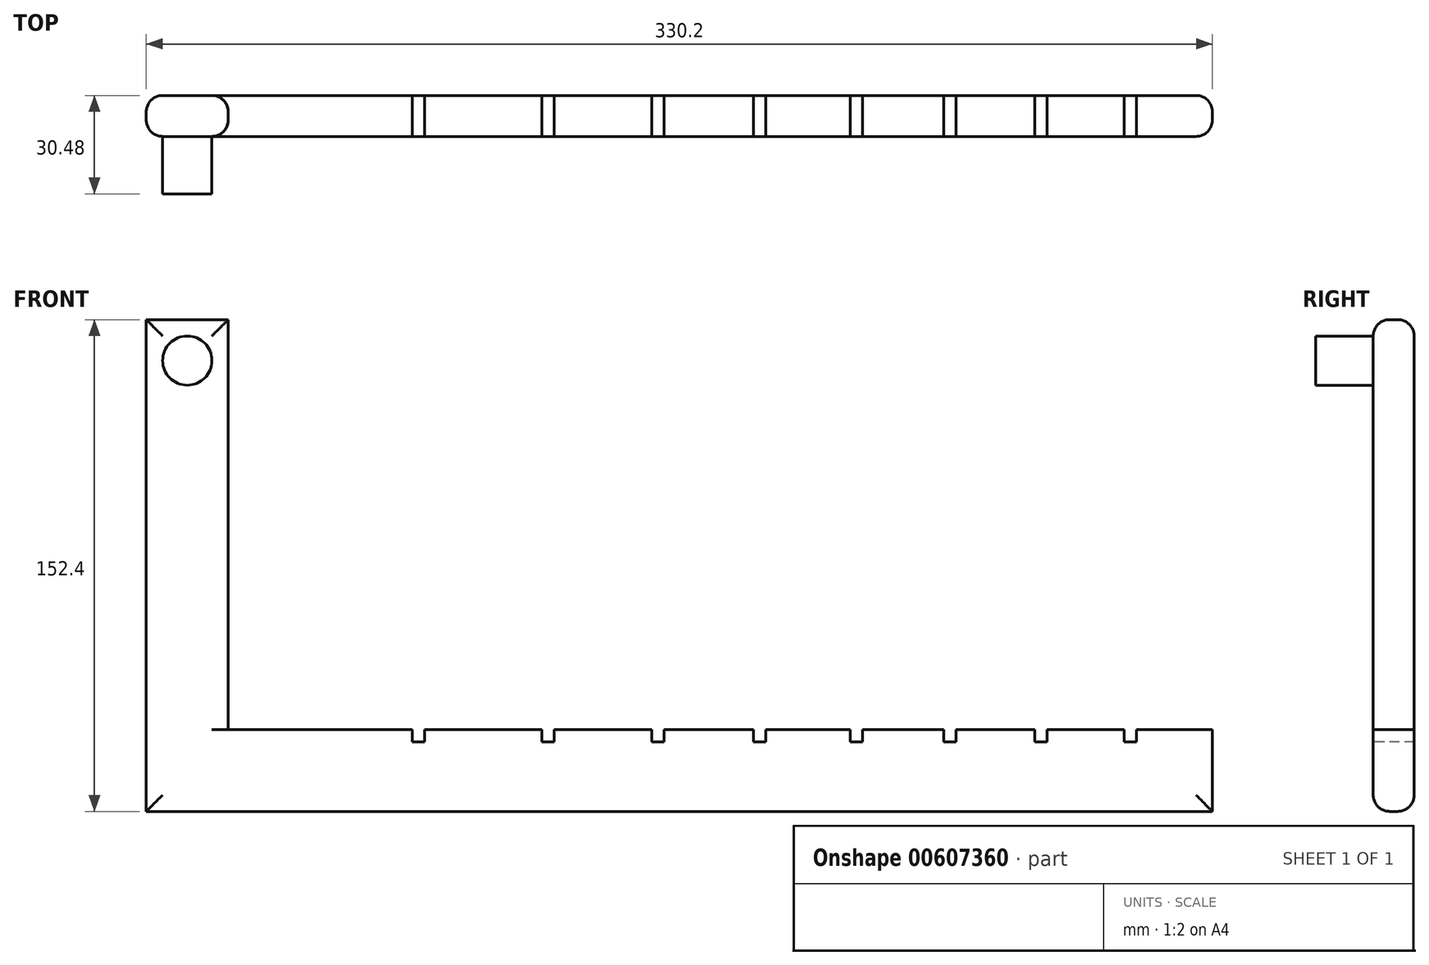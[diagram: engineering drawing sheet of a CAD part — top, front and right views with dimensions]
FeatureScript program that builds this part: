
annotation { "Feature Type Name" : "Feature", "Feature Type Description" : "" }
export const myFeature = defineFeature(function(context is Context, id is Id, definition is map)
    precondition{}
    {
        {
            var Q0;
            Q0=qCreatedBy(makeId("Front.planeOp"),FACE);
            var sketch = newSketch(context, id + "F0", { "sketchPlane" : qUnion([Q0])});
            skLineSegment(sketch, "E0.bottom", {"start": v(0, 0) * mm, "end": v(330.2, 0) * mm});
            skLineSegment(sketch, "E0.top", {"start": v(0, -25.4) * mm, "end": v(330.2, -25.4) * mm});
            skLineSegment(sketch, "E0.left", {"start": v(0, 0) * mm, "end": v(0, -25.4) * mm});
            skLineSegment(sketch, "E0.right", {"start": v(330.2, 0) * mm, "end": v(330.2, -25.4) * mm});
            skLineSegment(sketch, "E1.bottom", {"start": v(0, 0) * mm, "end": v(25.4, 0) * mm});
            skLineSegment(sketch, "E1.top", {"start": v(0, 127) * mm, "end": v(25.4, 127) * mm});
            skLineSegment(sketch, "E1.left", {"start": v(0, 0) * mm, "end": v(0, 127) * mm});
            skLineSegment(sketch, "E1.right", {"start": v(25.4, 0) * mm, "end": v(25.4, 127) * mm});
            skSolve(sketch);
        }
        {
            var Q0;
            Q0 = qSketchRegion(id + "F0", true);
            extrude(context, id + "F1", {"entities" : qUnion([Q0]), "depth" : 12.7 * mm, "offsetDistance" : 25.4 * mm});
        }
        {
            var Q0;
            Q0=makeQuery(id+"F1.opExtrude","CAP_FACE",FACE,{"disambiguationData":[OSD([sQuery(id+"F0.wireOp",EDGE,"E0.bottom"),sQuery(id+"F0.wireOp",EDGE,"E0.top"),sQuery(id+"F0.wireOp",EDGE,"E0.left"),sQuery(id+"F0.wireOp",EDGE,"E0.right"),sQuery(id+"F0.wireOp",EDGE,"E1.top"),sQuery(id+"F0.wireOp",EDGE,"E1.left"),sQuery(id+"F0.wireOp",EDGE,"E1.right")])],"isStart":false});
            var sketch = newSketch(context, id + "F2", { "sketchPlane" : qUnion([Q0])});
            skPoint(sketch, "E2", {"position": v(12.7, 127) * mm});
            skLineSegment(sketch, "E3", {"start": v(12.7, 127) * mm, "end": v(12.7, 114.3) * mm});
            skCircle(sketch, "E4", {"center": v(12.7, 114.3) * mm, "radius": 7.62 * mm});
            skSolve(sketch);
        }
        {
            var Q0;
            Q0 = qSketchRegion(id + "F2", true);
            extrude(context, id + "F3", {"entities" : qUnion([Q0]), "operationType" : NewBodyOperationType.ADD, "depth" : 17.78 * mm, "offsetDistance" : 25.4 * mm});
        }
        {
            var Q0;
            Q0=makeQuery(id+"F1.opExtrude","CAP_FACE",FACE,{"disambiguationData":[OSD([sQuery(id+"F0.wireOp",EDGE,"E0.bottom"),sQuery(id+"F0.wireOp",EDGE,"E0.top"),sQuery(id+"F0.wireOp",EDGE,"E0.left"),sQuery(id+"F0.wireOp",EDGE,"E0.right"),sQuery(id+"F0.wireOp",EDGE,"E1.top"),sQuery(id+"F0.wireOp",EDGE,"E1.left"),sQuery(id+"F0.wireOp",EDGE,"E1.right")])],"isStart":false});
            var sketch = newSketch(context, id + "F4", { "sketchPlane" : qUnion([Q0])});
            skLineSegment(sketch, "E5", {"start": v(25.4, 0) * mm, "end": v(84.33, 0) * mm});
            skLineSegment(sketch, "E6", {"start": v(25.4, 0) * mm, "end": v(124.46, 0) * mm});
            skLineSegment(sketch, "E7", {"start": v(25.4, 0) * mm, "end": v(158.5, 0) * mm});
            skLineSegment(sketch, "E8", {"start": v(25.4, 0) * mm, "end": v(190, 0) * mm});
            skLineSegment(sketch, "E9", {"start": v(25.4, 0) * mm, "end": v(219.96, 0) * mm});
            skLineSegment(sketch, "E10", {"start": v(25.4, 0) * mm, "end": v(248.92, 0) * mm});
            skLineSegment(sketch, "E11", {"start": v(25.4, 0) * mm, "end": v(277.11, 0) * mm});
            skLineSegment(sketch, "E12", {"start": v(25.4, 0) * mm, "end": v(304.8, 0) * mm});
            skLineSegment(sketch, "E13.bottom", {"start": v(86.23, -3.8) * mm, "end": v(82.42, -3.8) * mm});
            skLineSegment(sketch, "E13.top", {"start": v(86.23, 3.81) * mm, "end": v(82.42, 3.81) * mm});
            skLineSegment(sketch, "E13.left", {"start": v(86.23, -3.8) * mm, "end": v(86.23, 3.81) * mm});
            skLineSegment(sketch, "E13.right", {"start": v(82.42, -3.8) * mm, "end": v(82.42, 3.81) * mm});
            skPoint(sketch, "E13.middle", {"position": v(84.33, 0) * mm});
            skLineSegment(sketch, "E14.bottom", {"start": v(126.37, -3.8) * mm, "end": v(122.56, -3.8) * mm});
            skLineSegment(sketch, "E14.top", {"start": v(126.37, 3.81) * mm, "end": v(122.56, 3.81) * mm});
            skLineSegment(sketch, "E14.left", {"start": v(126.37, -3.8) * mm, "end": v(126.37, 3.81) * mm});
            skLineSegment(sketch, "E14.right", {"start": v(122.56, -3.8) * mm, "end": v(122.56, 3.81) * mm});
            skPoint(sketch, "E14.middle", {"position": v(124.46, 0) * mm});
            skLineSegment(sketch, "E15.bottom", {"start": v(160.4, -3.8) * mm, "end": v(156.6, -3.8) * mm});
            skLineSegment(sketch, "E15.top", {"start": v(160.4, 3.81) * mm, "end": v(156.6, 3.81) * mm});
            skLineSegment(sketch, "E15.left", {"start": v(160.4, -3.8) * mm, "end": v(160.4, 3.81) * mm});
            skLineSegment(sketch, "E15.right", {"start": v(156.6, -3.8) * mm, "end": v(156.6, 3.81) * mm});
            skPoint(sketch, "E15.middle", {"position": v(158.5, 0) * mm});
            skLineSegment(sketch, "E16.bottom", {"start": v(191.9, -3.8) * mm, "end": v(188.09, -3.8) * mm});
            skLineSegment(sketch, "E16.top", {"start": v(191.9, 3.81) * mm, "end": v(188.09, 3.81) * mm});
            skLineSegment(sketch, "E16.left", {"start": v(191.9, -3.8) * mm, "end": v(191.9, 3.81) * mm});
            skLineSegment(sketch, "E16.right", {"start": v(188.09, -3.8) * mm, "end": v(188.09, 3.81) * mm});
            skPoint(sketch, "E16.middle", {"position": v(190, 0) * mm});
            skLineSegment(sketch, "E17.bottom", {"start": v(221.87, -3.8) * mm, "end": v(218.06, -3.8) * mm});
            skLineSegment(sketch, "E17.top", {"start": v(221.87, 3.81) * mm, "end": v(218.06, 3.81) * mm});
            skLineSegment(sketch, "E17.left", {"start": v(221.87, -3.8) * mm, "end": v(221.87, 3.81) * mm});
            skLineSegment(sketch, "E17.right", {"start": v(218.06, -3.8) * mm, "end": v(218.06, 3.81) * mm});
            skPoint(sketch, "E17.middle", {"position": v(219.96, 0) * mm});
            skLineSegment(sketch, "E18.bottom", {"start": v(250.83, -3.8) * mm, "end": v(247.02, -3.8) * mm});
            skLineSegment(sketch, "E18.top", {"start": v(250.83, 3.81) * mm, "end": v(247.02, 3.81) * mm});
            skLineSegment(sketch, "E18.left", {"start": v(250.83, -3.8) * mm, "end": v(250.83, 3.81) * mm});
            skLineSegment(sketch, "E18.right", {"start": v(247.02, -3.8) * mm, "end": v(247.02, 3.81) * mm});
            skPoint(sketch, "E18.middle", {"position": v(248.92, 0) * mm});
            skLineSegment(sketch, "E19.bottom", {"start": v(279.02, -3.8) * mm, "end": v(275.2, -3.8) * mm});
            skLineSegment(sketch, "E19.top", {"start": v(279.02, 3.81) * mm, "end": v(275.2, 3.81) * mm});
            skLineSegment(sketch, "E19.left", {"start": v(279.02, -3.8) * mm, "end": v(279.02, 3.81) * mm});
            skLineSegment(sketch, "E19.right", {"start": v(275.2, -3.8) * mm, "end": v(275.2, 3.81) * mm});
            skPoint(sketch, "E19.middle", {"position": v(277.11, 0) * mm});
            skLineSegment(sketch, "E20.bottom", {"start": v(306.7, -3.8) * mm, "end": v(302.9, -3.8) * mm});
            skLineSegment(sketch, "E20.top", {"start": v(306.7, 3.81) * mm, "end": v(302.9, 3.81) * mm});
            skLineSegment(sketch, "E20.left", {"start": v(306.7, -3.8) * mm, "end": v(306.7, 3.81) * mm});
            skLineSegment(sketch, "E20.right", {"start": v(302.9, -3.8) * mm, "end": v(302.9, 3.81) * mm});
            skPoint(sketch, "E20.middle", {"position": v(304.8, 0) * mm});
            skSolve(sketch);
        }
        {
            var Q0;
            Q0 = qSketchRegion(id + "F4", true);
            extrude(context, id + "F5", {"entities" : qUnion([Q0]), "operationType" : NewBodyOperationType.REMOVE, "oppositeDirection" : true, "depth" : 25.4 * mm, "offsetDistance" : 25.4 * mm});
        }
        {
            var Q0;
            Q0=makeQuery(id+"F1.opExtrude","CAP_EDGE",EDGE,{"disambiguationData":[OSD([sQuery(id+"F0.wireOp",EDGE,"E0.top")])],"isStart":false});
            var Q1;
            Q1=makeQuery(id+"F1.opExtrude","CAP_EDGE",EDGE,{"disambiguationData":[OSD([sQuery(id+"F0.wireOp",EDGE,"E0.top")])],"isStart":true});
            var Q2;
            Q2=makeQuery(id+"F1.opExtrude","CAP_EDGE",EDGE,{"disambiguationData":[OSD([sQuery(id+"F0.wireOp",EDGE,"E0.left"),sQuery(id+"F0.wireOp",EDGE,"E1.left")])],"isStart":true});
            var Q3;
            Q3=makeQuery(id+"F1.opExtrude","CAP_EDGE",EDGE,{"disambiguationData":[OSD([sQuery(id+"F0.wireOp",EDGE,"E0.left"),sQuery(id+"F0.wireOp",EDGE,"E1.left")])],"isStart":false});
            var Q4;
            Q4=makeQuery(id+"F1.opExtrude","CAP_EDGE",EDGE,{"disambiguationData":[OSD([sQuery(id+"F0.wireOp",EDGE,"E1.top")])],"isStart":true});
            var Q5;
            Q5=makeQuery(id+"F1.opExtrude","CAP_EDGE",EDGE,{"disambiguationData":[OSD([sQuery(id+"F0.wireOp",EDGE,"E1.top")])],"isStart":false});
            var Q6;
            Q6=makeQuery(id+"F1.opExtrude","CAP_EDGE",EDGE,{"disambiguationData":[OSD([sQuery(id+"F0.wireOp",EDGE,"E1.right")])],"isStart":true});
            var Q7;
            Q7=makeQuery(id+"F1.opExtrude","CAP_EDGE",EDGE,{"disambiguationData":[OSD([sQuery(id+"F0.wireOp",EDGE,"E1.right")])],"isStart":false});
            var Q8;
            Q8=makeQuery(id+"F1.opExtrude","CAP_EDGE",EDGE,{"disambiguationData":[OSD([sQuery(id+"F0.wireOp",EDGE,"E0.right")])],"isStart":true});
            var Q9;
            Q9=makeQuery(id+"F1.opExtrude","CAP_EDGE",EDGE,{"disambiguationData":[OSD([sQuery(id+"F0.wireOp",EDGE,"E0.right")])],"isStart":false});
            fillet(context, id + "F6", {"entities" : qUnion([Q0, Q1, Q2, Q3, Q4, Q5, Q6, Q7, Q8, Q9]), "radius" : 5.08 * mm, "tangentPropagation" : true, "allowEdgeOverflow" : false});
        }
    });
